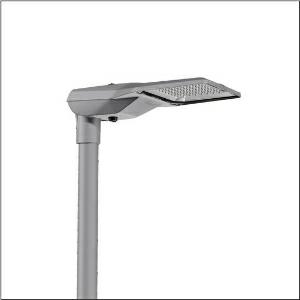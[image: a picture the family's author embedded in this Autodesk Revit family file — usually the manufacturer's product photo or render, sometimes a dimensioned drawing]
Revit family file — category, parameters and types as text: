
# Revit family: streetlight_sl_21_iq_midi___p0_8a_5xe3u31y08mb_3be5
name_source: partatom
category: Lighting Fixtures
units: mm (PartAtom-declared; Revit-internal decimal feet)

## family parameters
Cut with Voids When Loaded = No
Host = Face
Light Source = No
Part Type = Normal
Room Calculation Point = No
Round Connector Dimension = Use Diameter
Shared = No

## types (1)
- --- (1 x LED, 18500 lm, 129.3 W, 3000K)
    Apparent Load = 129 VA
    CIE Flux Codes = 33 69 96 100 100
    Color Rendering = 70
    Color Temperature = 3000K
    Default Elevation = 1800 mm
    Description = Streetlight SL 21 iQ midi, mast luminaire, primary light control with lens, of PMMA, primary optical cover: cover, of toughened safety glass, transparent, light distribution: P0.8a, light emission: direct distribution, primary light characteristic: asymmetric, installation type: post-top, side-entry, LED, High Power LED, rated luminous flux: 18.500lm, luminous efficacy: 143lm/W, light colour: 730, colour temperature: 3000K, control gear: iQ-Street Remote, D4i with power reduction, control: pre-setting: logarithmic dimming characteristic, Street-Remote, Auto-Match, Temp-Guard, Lumen-Switch, Night-Set, Smart-Wire, Light-Fading, Desk-Remote (wireless, voltage-free reading and setting of iQ features in the workshop via application-optimized NFC function/RFID function), optimised constant luminous flux control (CLO 2.0), mains connection: 230..240V, AC, 50/60Hz, start of lifetime: 129W, end of service life: 142W, reduction: 56W, luminaire housing, of diecast aluminium, powder-coated, SITECO metallic grey (DB 702S), corrosivity category C5 high according to DIN EN ISO 12944, please order mast flange separately, inclination adjustable: 0°, 5°, 10°, 15°, sealing non-destructively replaceable, multi-level sealing system, length: 644mm, width: 335mm, height: 110mm, mast flange for spigot size: 42mm (side-entry): 5XC10008XM4, 60/48mm (side-entry/post-top): 5XC10108XM2, 76/60mm (side-entry/post-top): 5XC10108XM1, mounting height: 4..8m, Smart Interface below and above, protection rating (complete): IP66, insulation class (complete): insulation class II (safety insulation), certification: CE, ENEC, ENEC+, VDE, impact resistance: IK10, permissible operating ambient temperature for outdoor applications: -40..+50°C, standard-compliant lighting for roads and squares, packaging unit: 1 piece

Light Distribution: P0.8a
    Height = 111 mm
    Lamp = 1 x LED
    Lamp Light Flux = 18500 lm
    Lamp Power = 129.3 W
    Lamp count = 1
    Length = 644 mm
    Luminous efficacy = 143 lm/W
    Manufacturer = Siteco
    ModVariant = No
    Model = 5XE3U31Y08MB
    Number of Poles = 1
    OnlyDefault = Yes
    Power Factor = 1
    Product Name = Streetlight SL 21 iQ midi | P0.8a
    Product group = mast luminaire | pylon top
    ProductGroupID = 6100
    Protection Class = Protection class II
    Protection Degree = IP 66
    RLX_Detail_Level = 1
    RLX_Emergency_Light_Flux = 0 lm
    RLX_Emergency_Type = 0
    RLX_Emergency_Type_DB = No
    RlxData = <blob elided: 90869 chars, md5=39d7383f>
    Socket = socket
    Standby Power = 0 W
    System Light Flux = 18500 lm
    System Power = 129 W
    Type Comments = factory setting: luminous flux: 100 % | dim-lin: 254 | 672 mA
    Type Image = l_1004304.jpg
    URL = http://relux.com
    VarID = @adj_081649
    Voltage = 0 V
    Weight = 0.00 kg
    Width = 336 mm

## geometry (parser evidence)
native form markers: Blend x4, Sweep x11
no freeform markers — native parametric forms only
